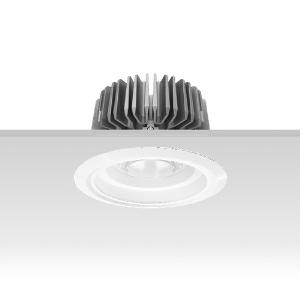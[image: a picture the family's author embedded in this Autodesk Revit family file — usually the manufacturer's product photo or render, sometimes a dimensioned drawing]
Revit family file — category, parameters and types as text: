
# Revit family: 3f_filippi_-_3f_reno_bianco_ampio_3f_filippi_-_30362_a01023_-_3f_reno_150_wh_2000-930_ep_wide___vt_wh_8b1e
name_source: partatom
category: Lighting Fixtures
units: mm (PartAtom-declared; Revit-internal decimal feet)

## family parameters
Cut with Voids When Loaded = No
Host = Face
Light Source = No
Part Type = Normal
Room Calculation Point = No
Round Connector Dimension = Use Diameter
Shared = No

## types (1)
- 3F Filippi - 3F Reno Bianco Ampio (1 x LED, 1888 lm, 25 W, 3000 K)
    Apparent Load = 25 VA
    Approval mark = ENEC
    CIE Flux Codes = 74 93 99 100 100
    Color Rendering = 90
    Color Temperature = 3000 K
    Control Gear = Electronic ballast
    Default Elevation = 1800 mm
    Description = ILLUMINOTECHNICAL
Luminous efficiency 100% (DLOR 100%, ULOR 0%).
Initial luminous flux of the luminaire 1888 lm.
Emergency luminaire luminous flux BLF 16.7%.
Direct symmetric wide distribution.
Installation Interdistance Transv.D = 1.54 x hu - Long.D = 1.54 x hu.
Tabular UGR (CIE 117 - 4H-8H; S=0.25H; 70/50/20): RUG 23.2 - 23.
Beam angle: 74° - 73°.
Luminous efficacy 76 lm/W.
Lifetime (L90/B10): 30000 h. (tq+25°C)
Lifetime (L85/B10): 50000 h. (tq+25°C)
Lifetime (L70/B10): 80000 h. (tq+25°C)
Sudden decreased luminous flux after 50000 hours: 0% (C0).
Photobiological safety in compliance with IEC/TR 62778: RG0 risk exempt, (IEC 62471).
In compliance with IEC/EN 62722-2-1 - IEC/EN 62717 standards.

SOURCE
Compact LED module 2000/930.
Energy efficiency class (UE 2019/2020 - UE 2019/2015): E.
CIE 13.3 Colour rendering index: CRI >90 (R9 >50%).
IES TM-30 Fidelity Index: Rf = 92 Rg = 101.
CCT nominal colour temperature 3000 K.
Colour initial tolerance (MacAdam): SDCM 3.
Zhaga Book 3 compliant.

MECHANICAL
Passive heat dissipator in die-casting aluminium, oversized, for optimum thermal management of the LED module.
Parabolic element with graduated/concentric rings in white polycarbonate.
Transparent external lens with glossy and satin differentiated surfaces, with a cooling and anti-insect system in methacrylate (PMMA).
Fastening spring clips in stainless steel.
Dimensions: diameter 176 mm, height 111 mm. Weight 1.35 kg.
IP44 protection degree for exposed part, IP20 for recessed part.
Mechanical strength to impacts IK06 (1 joule).
Glow-wire test resistance 650°C.

ELECTRICAL
Wiring on a separate unit.
Halogen Free electronic wiring 230V-50/60Hz, power factor 0.90, THD <25%, constant output current, SELV, class II, 1 driver.
Power of the luminaire 25 W.
CE - IEC 60598-1 - EN 60598-1.
EP maintained emergency wiring on board, 1h duration, 24h recharge; compliant with EN 60598-2-22, excluding high risk areas.
SAFE FLICKER: PstLM=<1 and SVM=<0.4 (IEC TR 61547-1 and IEC TR 63158), to ensure a more comfortable and safe light.
Ambient temperature from +5°C to +25°C.
Temperature class T6 max 85°C.
Relative humidity UR: <85%.

INSTALLATION
Pull-up recessed fitting.
False ceiling carving: 150 mm.
All accessories dedicated to this product are available on the Catalog and on our website www.3F-Filippi.com.

ACCESSORIES
A01023 - VT transparent glass, tempered, not flammable, locked and in line with the trim, in white polycarbonate.

APPLICATIONS
Environments: architectural, commercial, exhibition areas, transit areas, corridors, shops, display windows, service areas.
In false ceilings with narrow voids.

WARNING
Luminaire designed for disposal/recycling at end-of-life.
Replaceable (LED only) light source by a professional. Replaceable control gear by a professional.
    Height = 0 mm  [stored 0 ft]
    Lamp = 1 x LED
    Lamp Light Flux = 1888 lm
    Lamp Power = 25 W
    Lamp count = 1
    Length = 176 mm
    Lifetime = 50000 h
    Luminous efficacy = 76 lm/W
    Manufacturer = 3F Filippi
    ModVariant = No
    Model = 3F Filippi - 30362+A01023 - 3F Reno 150 WH 2000-930 EP WIDE + VT WH
    Mounting Place = Ceiling
    Mounting Type = Recessed
    Number of Poles = 1
    OnlyDefault = Yes
    Power Factor = 1
    Product Name = 3F Filippi - 3F Reno Bianco Ampio
    Product group = recessed luminaire
    ProductGroupID = 4
    Protection Class = Protection class II
    Protection Degree = IP 20
    RLX_Detail_Level = 1
    RLX_Emergency_Light_Flux = 0 lm
    RLX_Emergency_Type = 0
    RLX_Emergency_Type_DB = No
    RlxData = <blob elided: 84873 chars, md5=665a766f>
    Socket = socket
    Standby Power = 0 W
    System Light Flux = 1888 lm
    System Power = 25 W
    Type Comments = Product without accessories
    Type Image = 3ffilippi_3f_reno_150_wh_d150__a01023.jpg
    URL = http://relux.com
    VarID = ---
    Voltage = 0 V
    Weight = 0.00 kg
    Width = 0 mm  [stored 0 ft]

note: [stored X ft] marks values corroborated as IEEE doubles in the binary element streams (Revit-internal decimal feet)

## geometry (parser evidence)
native form markers: Blend x4, Sweep x13
no freeform markers — native parametric forms only
